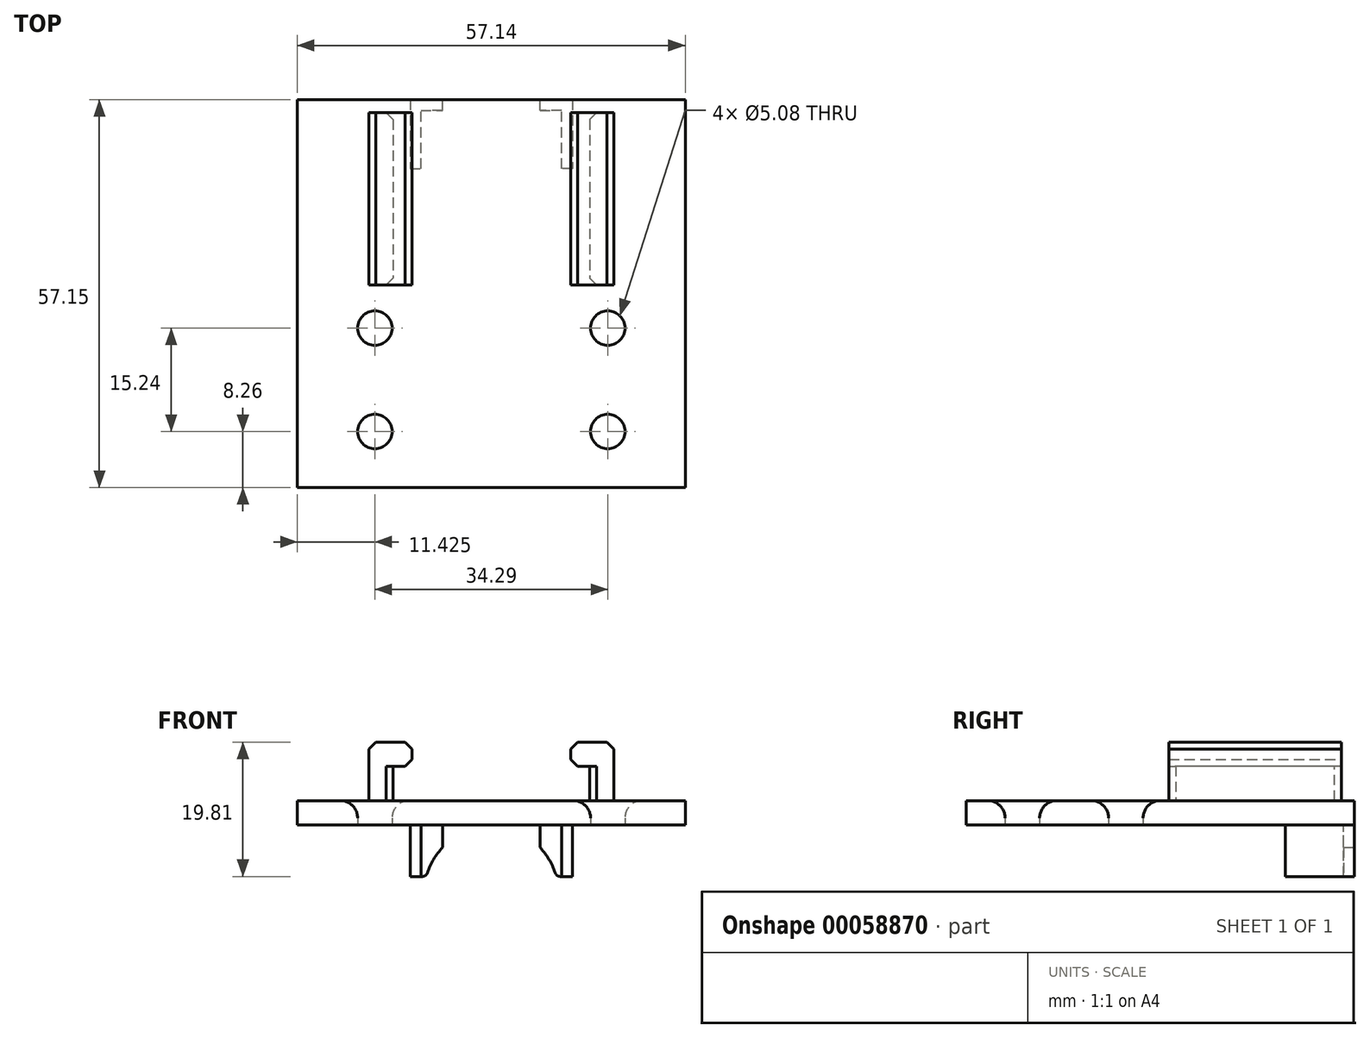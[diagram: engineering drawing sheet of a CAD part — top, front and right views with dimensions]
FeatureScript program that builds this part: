
annotation { "Feature Type Name" : "Feature", "Feature Type Description" : "" }
export const myFeature = defineFeature(function(context is Context, id is Id, definition is map)
    precondition{}
    {
        {
            var Q0;
            Q0=qCreatedBy(makeId("Top.planeOp"),FACE);
            var sketch = newSketch(context, id + "F0", { "sketchPlane" : qUnion([Q0])});
            skLineSegment(sketch, "E0.bottom", {"start": v(-28.58, 15.88) * mm, "end": v(28.58, 15.88) * mm});
            skLineSegment(sketch, "E0.top", {"start": v(-28.58, -15.88) * mm, "end": v(28.58, -15.88) * mm});
            skLineSegment(sketch, "E0.left", {"start": v(-28.58, 15.88) * mm, "end": v(-28.58, -15.88) * mm});
            skLineSegment(sketch, "E0.right", {"start": v(28.58, 15.87) * mm, "end": v(28.58, -15.87) * mm});
            skLineSegment(sketch, "E1", {"start": v(0, 15.88) * mm, "end": v(0, -15.88) * mm, "construction": true});
            skPoint(sketch, "E2", {"position": v(0, 0) * mm});
            skCircle(sketch, "E3", {"center": v(-17.15, 7.62) * mm, "radius": 2.54 * mm});
            skCircle(sketch, "E4.MirrorC", {"center": v(17.15, 7.62) * mm, "radius": 2.54 * mm});
            skCircle(sketch, "E5.MirrorC", {"center": v(-17.15, -7.62) * mm, "radius": 2.54 * mm});
            skCircle(sketch, "E6.MirrorC", {"center": v(17.15, -7.62) * mm, "radius": 2.54 * mm});
            skSolve(sketch);
        }
        {
            var Q0;
            Q0 = qSketchRegion(id + "F0", true);
            extrude(context, id + "F1", {"entities" : qUnion([Q0]), "depth" : 3.56 * mm});
        }
        {
            var Q0;
            Q0=qCreatedBy(makeId("Top.planeOp"),FACE);
            var sketch = newSketch(context, id + "F2", { "sketchPlane" : qUnion([Q0])});
            skLineSegment(sketch, "E7.bottom", {"start": v(-28.57, 15.88) * mm, "end": v(28.58, 15.88) * mm});
            skLineSegment(sketch, "E7.top", {"start": v(-28.58, 41.28) * mm, "end": v(28.58, 41.28) * mm});
            skLineSegment(sketch, "E7.left", {"start": v(-28.57, 15.88) * mm, "end": v(-28.58, 41.28) * mm});
            skLineSegment(sketch, "E7.right", {"start": v(28.58, 15.88) * mm, "end": v(28.58, 41.28) * mm});
            skSolve(sketch);
        }
        {
            var Q0;
            Q0 = qSketchRegion(id + "F2", true);
            extrude(context, id + "F3", {"entities" : qUnion([Q0]), "operationType" : NewBodyOperationType.ADD, "depth" : 3.56 * mm});
        }
        {
            var Q0;
            Q0=makeQuery(id+"F1.opExtrude","CAP_EDGE",EDGE,{"disambiguationData":[OSD([sQuery(id+"F0.wireOp",EDGE,"E3")])],"isStart":false});
            var Q1;
            Q1=makeQuery(id+"F1.opExtrude","CAP_EDGE",EDGE,{"disambiguationData":[OSD([sQuery(id+"F0.wireOp",EDGE,"E4.MirrorC")])],"isStart":false});
            var Q2;
            Q2=makeQuery(id+"F1.opExtrude","CAP_EDGE",EDGE,{"disambiguationData":[OSD([sQuery(id+"F0.wireOp",EDGE,"E6.MirrorC")])],"isStart":false});
            var Q3;
            Q3=makeQuery(id+"F1.opExtrude","CAP_EDGE",EDGE,{"disambiguationData":[OSD([sQuery(id+"F0.wireOp",EDGE,"E5.MirrorC")])],"isStart":false});
            fillet(context, id + "F4", {"entities" : qUnion([Q0, Q1, Q2, Q3]), "radius" : 2.54 * mm, "tangentPropagation" : true, "allowEdgeOverflow" : false});
        }
        {
            var Q0;
            Q0=makeQuery(id+"F3.boolean.opBoolean","MERGE",FACE,{"derivedFrom":[makeQuery(id+"F1.opExtrude","CAP_FACE",FACE,{"disambiguationData":[OSD([sQuery(id+"F0.wireOp",EDGE,"E0.bottom"),sQuery(id+"F0.wireOp",EDGE,"E0.top"),sQuery(id+"F0.wireOp",EDGE,"E0.left"),sQuery(id+"F0.wireOp",EDGE,"E0.right"),sQuery(id+"F0.wireOp",EDGE,"E3"),sQuery(id+"F0.wireOp",EDGE,"E4.MirrorC"),sQuery(id+"F0.wireOp",EDGE,"E5.MirrorC"),sQuery(id+"F0.wireOp",EDGE,"E6.MirrorC")])],"isStart":false}),makeQuery(id+"F3.opExtrude","CAP_FACE",FACE,{"disambiguationData":[OSD([sQuery(id+"F2.wireOp",EDGE,"E7.bottom"),sQuery(id+"F2.wireOp",EDGE,"E7.top"),sQuery(id+"F2.wireOp",EDGE,"E7.left"),sQuery(id+"F2.wireOp",EDGE,"E7.right")])],"isStart":false})]});
            var sketch = newSketch(context, id + "F5", { "sketchPlane" : qUnion([Q0])});
            skLineSegment(sketch, "E8.bottom", {"start": v(-18.03, 39.37) * mm, "end": v(-14.48, 39.37) * mm});
            skLineSegment(sketch, "E8.top", {"start": v(-18.03, 13.97) * mm, "end": v(-14.48, 13.97) * mm});
            skLineSegment(sketch, "E8.left", {"start": v(-18.03, 39.37) * mm, "end": v(-18.03, 13.97) * mm});
            skLineSegment(sketch, "E8.right", {"start": v(-14.48, 39.37) * mm, "end": v(-14.48, 13.97) * mm});
            skLineSegment(sketch, "E9.MirrorCS", {"start": v(18.03, 13.97) * mm, "end": v(14.48, 13.97) * mm});
            skLineSegment(sketch, "E10.MirrorCS", {"start": v(14.48, 39.37) * mm, "end": v(14.48, 13.97) * mm});
            skLineSegment(sketch, "E11.MirrorCS", {"start": v(18.03, 39.37) * mm, "end": v(14.48, 39.37) * mm});
            skLineSegment(sketch, "E12.MirrorCS", {"start": v(18.03, 39.37) * mm, "end": v(18.03, 13.97) * mm});
            skSolve(sketch);
        }
        {
            var Q0;
            Q0 = qSketchRegion(id + "F5", true);
            extrude(context, id + "F6", {"entities" : qUnion([Q0]), "operationType" : NewBodyOperationType.ADD, "depth" : 5.08 * mm});
        }
        {
            var Q0;
            Q0=makeQuery(id+"F6.opExtrude","CAP_FACE",FACE,{"disambiguationData":[OSD([sQuery(id+"F5.wireOp",EDGE,"E8.bottom"),sQuery(id+"F5.wireOp",EDGE,"E8.top"),sQuery(id+"F5.wireOp",EDGE,"E8.left"),sQuery(id+"F5.wireOp",EDGE,"E8.right")])],"isStart":false});
            var sketch = newSketch(context, id + "F7", { "sketchPlane" : qUnion([Q0])});
            skLineSegment(sketch, "E13.bottom", {"start": v(-18.03, 39.37) * mm, "end": v(-11.68, 39.37) * mm});
            skLineSegment(sketch, "E13.top", {"start": v(-18.03, 13.97) * mm, "end": v(-11.68, 13.97) * mm});
            skLineSegment(sketch, "E13.left", {"start": v(-18.03, 39.37) * mm, "end": v(-18.03, 13.97) * mm});
            skLineSegment(sketch, "E13.right", {"start": v(-11.68, 39.37) * mm, "end": v(-11.68, 13.97) * mm});
            skLineSegment(sketch, "E14.bottom", {"start": v(18.03, 39.37) * mm, "end": v(11.68, 39.37) * mm});
            skLineSegment(sketch, "E14.top", {"start": v(18.03, 13.97) * mm, "end": v(11.68, 13.97) * mm});
            skLineSegment(sketch, "E14.left", {"start": v(18.03, 39.37) * mm, "end": v(18.03, 13.97) * mm});
            skLineSegment(sketch, "E14.right", {"start": v(11.68, 39.37) * mm, "end": v(11.68, 13.97) * mm});
            skSolve(sketch);
        }
        {
            var Q0;
            Q0 = qSketchRegion(id + "F7", true);
            extrude(context, id + "F8", {"entities" : qUnion([Q0]), "operationType" : NewBodyOperationType.ADD, "depth" : 3.56 * mm});
        }
        {
            var Q0;
            Q0=makeQuery(id+"F8.opExtrude","CAP_EDGE",EDGE,{"disambiguationData":[OSD([sQuery(id+"F7.wireOp",EDGE,"E13.right")])],"isStart":false});
            var Q1;
            Q1=makeQuery(id+"F8.opExtrude","CAP_EDGE",EDGE,{"disambiguationData":[OSD([sQuery(id+"F7.wireOp",EDGE,"E13.right")])],"isStart":true});
            var Q2;
            Q2=makeQuery(id+"F8.opExtrude","CAP_EDGE",EDGE,{"disambiguationData":[OSD([sQuery(id+"F7.wireOp",EDGE,"E14.right")])],"isStart":false});
            var Q3;
            Q3=makeQuery(id+"F8.opExtrude","CAP_EDGE",EDGE,{"disambiguationData":[OSD([sQuery(id+"F7.wireOp",EDGE,"E14.right")])],"isStart":true});
            var Q4;
            Q4=makeQuery(id+"F8.opExtrude","CAP_EDGE",EDGE,{"disambiguationData":[OSD([sQuery(id+"F7.wireOp",EDGE,"E14.left")])],"isStart":false});
            var Q5;
            Q5=makeQuery(id+"F8.opExtrude","CAP_EDGE",EDGE,{"disambiguationData":[OSD([sQuery(id+"F7.wireOp",EDGE,"E13.left")])],"isStart":false});
            var Q6;
            Q6=makeQuery(id+"F6.opExtrude","CAP_EDGE",EDGE,{"disambiguationData":[OSD([sQuery(id+"F5.wireOp",EDGE,"E12.MirrorCS")])],"isStart":true});
            var Q7;
            Q7=makeQuery(id+"F6.opExtrude","CAP_EDGE",EDGE,{"disambiguationData":[OSD([sQuery(id+"F5.wireOp",EDGE,"E8.left")])],"isStart":true});
            var Q8;
            Q8=makeQuery(id+"F6.opExtrude","SWEPT_EDGE",EDGE,{"disambiguationData":[OSD([sQuery(id+"F5.wireOp",EDGE,"E10.MirrorCS"),sQuery(id+"F5.wireOp",EDGE,"E11.MirrorCS")])]});
            var Q9;
            Q9=makeQuery(id+"F6.opExtrude","SWEPT_EDGE",EDGE,{"disambiguationData":[OSD([sQuery(id+"F5.wireOp",EDGE,"E8.bottom"),sQuery(id+"F5.wireOp",EDGE,"E8.right")])]});
            var Q10;
            Q10=makeQuery(id+"F6.opExtrude","SWEPT_EDGE",EDGE,{"disambiguationData":[OSD([sQuery(id+"F5.wireOp",EDGE,"E8.top"),sQuery(id+"F5.wireOp",EDGE,"E8.right")])]});
            var Q11;
            Q11=makeQuery(id+"F6.opExtrude","SWEPT_EDGE",EDGE,{"disambiguationData":[OSD([sQuery(id+"F5.wireOp",EDGE,"E9.MirrorCS"),sQuery(id+"F5.wireOp",EDGE,"E10.MirrorCS")])]});
            chamfer(context, id + "F9", {"entities" : qUnion([Q0, Q1, Q2, Q3, Q4, Q5, Q6, Q7, Q8, Q9, Q10, Q11]), "width" : 1.02 * mm, "tangentPropagation" : true});
        }
        {
            var Q0;
            Q0=makeQuery(id+"F3.boolean.opBoolean","MERGE",FACE,{"derivedFrom":[makeQuery(id+"F1.opExtrude","CAP_FACE",FACE,{"disambiguationData":[OSD([sQuery(id+"F0.wireOp",EDGE,"E0.bottom"),sQuery(id+"F0.wireOp",EDGE,"E0.top"),sQuery(id+"F0.wireOp",EDGE,"E0.left"),sQuery(id+"F0.wireOp",EDGE,"E0.right"),sQuery(id+"F0.wireOp",EDGE,"E3"),sQuery(id+"F0.wireOp",EDGE,"E4.MirrorC"),sQuery(id+"F0.wireOp",EDGE,"E5.MirrorC"),sQuery(id+"F0.wireOp",EDGE,"E6.MirrorC")])],"isStart":true}),makeQuery(id+"F3.opExtrude","CAP_FACE",FACE,{"disambiguationData":[OSD([sQuery(id+"F2.wireOp",EDGE,"E7.bottom"),sQuery(id+"F2.wireOp",EDGE,"E7.top"),sQuery(id+"F2.wireOp",EDGE,"E7.left"),sQuery(id+"F2.wireOp",EDGE,"E7.right")])],"isStart":true})]});
            var sketch = newSketch(context, id + "F10", { "sketchPlane" : qUnion([Q0])});
            skLineSegment(sketch, "E15", {"start": v(-7.16, -41.28) * mm, "end": v(-11.96, -41.28) * mm});
            skLineSegment(sketch, "E16", {"start": v(-11.96, -41.28) * mm, "end": v(-11.96, -31.12) * mm});
            skLineSegment(sketch, "E17", {"start": v(-11.96, -31.12) * mm, "end": v(-10.36, -31.12) * mm});
            skLineSegment(sketch, "E18", {"start": v(-10.36, -31.12) * mm, "end": v(-10.36, -39.68) * mm});
            skLineSegment(sketch, "E19", {"start": v(-10.36, -39.68) * mm, "end": v(-7.16, -39.68) * mm});
            skLineSegment(sketch, "E20", {"start": v(-7.16, -39.68) * mm, "end": v(-7.16, -41.28) * mm});
            skLineSegment(sketch, "E21", {"start": v(0, -41.28) * mm, "end": v(0, -20.22) * mm, "construction": true});
            skPoint(sketch, "E21.endSnap0", {"position": v(0, -41.28) * mm});
            skLineSegment(sketch, "E22.MirrorCS", {"start": v(10.36, -39.68) * mm, "end": v(7.16, -39.68) * mm});
            skLineSegment(sketch, "E23.MirrorCS", {"start": v(7.16, -39.68) * mm, "end": v(7.16, -41.28) * mm});
            skLineSegment(sketch, "E24.MirrorCS", {"start": v(7.16, -41.28) * mm, "end": v(11.96, -41.28) * mm});
            skLineSegment(sketch, "E25.MirrorCS", {"start": v(11.96, -41.28) * mm, "end": v(11.96, -31.12) * mm});
            skLineSegment(sketch, "E26.MirrorCS", {"start": v(10.36, -31.12) * mm, "end": v(10.36, -39.68) * mm});
            skLineSegment(sketch, "E27.MirrorCS", {"start": v(11.96, -31.12) * mm, "end": v(10.36, -31.12) * mm});
            skSolve(sketch);
        }
        {
            var Q0;
            Q0 = qSketchRegion(id + "F10", true);
            extrude(context, id + "F11", {"entities" : qUnion([Q0]), "operationType" : NewBodyOperationType.ADD, "depth" : 7.62 * mm});
        }
        {
            var Q0;
            Q0=makeQuery(id+"F11.boolean.opBoolean","MERGE",FACE,{"derivedFrom":[makeQuery(id+"F3.opExtrude","SWEPT_FACE",FACE,{"disambiguationData":[OSD([sQuery(id+"F2.wireOp",EDGE,"E7.top")])]}),makeQuery(id+"F11.opExtrude","SWEPT_FACE",FACE,{"disambiguationData":[OSD([sQuery(id+"F10.wireOp",EDGE,"E15")])]}),makeQuery(id+"F11.opExtrude","SWEPT_FACE",FACE,{"disambiguationData":[OSD([sQuery(id+"F10.wireOp",EDGE,"E24.MirrorCS")])]})]});
            var sketch = newSketch(context, id + "F12", { "sketchPlane" : qUnion([Q0])});
            skLineSegment(sketch, "E28", {"start": v(0, 0) * mm, "end": v(0, 3.56) * mm, "construction": true});
            skLineSegment(sketch, "E29", {"start": v(0, 0) * mm, "end": v(0, -10.16) * mm, "construction": true});
            skCircle(sketch, "E30", {"center": v(0, -10.16) * mm, "radius": 9.9 * mm});
            skPoint(sketch, "E31", {"position": v(-9.56, -7.62) * mm});
            skSolve(sketch);
        }
        {
            var Q0;
            Q0 = qSketchRegion(id + "F12", true);
            extrude(context, id + "F13", {"entities" : qUnion([Q0]), "operationType" : NewBodyOperationType.REMOVE, "oppositeDirection" : true, "depth" : 25.4 * mm});
        }
        {
            var Q0;
            Q0=makeQuery(id+"F13.boolean.opBoolean","INTERSECT",EDGE,{"derivedFrom":[makeQuery(id+"F11.opExtrude","CAP_FACE",FACE,{"disambiguationData":[OSD([sQuery(id+"F10.wireOp",EDGE,"E22.MirrorCS"),sQuery(id+"F10.wireOp",EDGE,"E23.MirrorCS"),sQuery(id+"F10.wireOp",EDGE,"E24.MirrorCS"),sQuery(id+"F10.wireOp",EDGE,"E25.MirrorCS"),sQuery(id+"F10.wireOp",EDGE,"E26.MirrorCS"),sQuery(id+"F10.wireOp",EDGE,"E27.MirrorCS")])],"isStart":false}),makeQuery(id+"F13.opExtrude","SWEPT_FACE",FACE,{"disambiguationData":[OSD([sQuery(id+"F12.wireOp",EDGE,"E30")])]})]});
            var Q1;
            Q1=makeQuery(id+"F13.boolean.opBoolean","INTERSECT",EDGE,{"derivedFrom":[makeQuery(id+"F11.opExtrude","CAP_FACE",FACE,{"disambiguationData":[OSD([sQuery(id+"F10.wireOp",EDGE,"E15"),sQuery(id+"F10.wireOp",EDGE,"E16"),sQuery(id+"F10.wireOp",EDGE,"E17"),sQuery(id+"F10.wireOp",EDGE,"E18"),sQuery(id+"F10.wireOp",EDGE,"E19"),sQuery(id+"F10.wireOp",EDGE,"E20")])],"isStart":false}),makeQuery(id+"F13.opExtrude","SWEPT_FACE",FACE,{"disambiguationData":[OSD([sQuery(id+"F12.wireOp",EDGE,"E30")])]})]});
            var Q2;
            Q2=makeQuery(id+"F11.opExtrude","CAP_EDGE",EDGE,{"disambiguationData":[OSD([sQuery(id+"F10.wireOp",EDGE,"E20")])],"isStart":true});
            var Q3;
            Q3=makeQuery(id+"F11.opExtrude","CAP_EDGE",EDGE,{"disambiguationData":[OSD([sQuery(id+"F10.wireOp",EDGE,"E23.MirrorCS")])],"isStart":true});
            fillet(context, id + "F14", {"entities" : qUnion([Q0, Q1, Q2, Q3]), "radius" : .8 * mm, "tangentPropagation" : true, "allowEdgeOverflow" : false});
        }
    });
